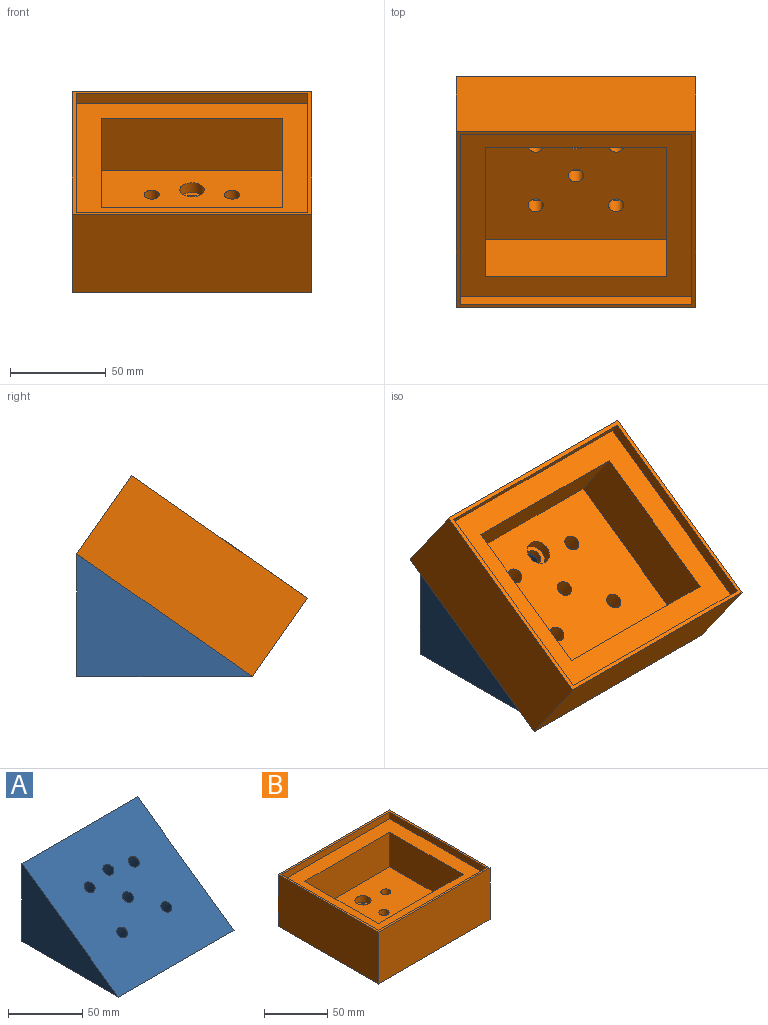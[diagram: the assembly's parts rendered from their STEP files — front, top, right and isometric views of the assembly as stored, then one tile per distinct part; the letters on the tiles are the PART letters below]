
ASSEMBLY  parts=2 mates=1
PART A: 34 faces, bbox 110x91.8x64.2 mm
  f0: plane 60x36mm, normal (0,0,-1), area 1964.4mm2, adj f5,f10,f11,f12,f21,f22,f23,f24
  f1: cylinder r=4mm len=21.79mm, axis (0,-0.57,0.82), area 481.3mm2, adj f7,f26,f30,f31
  f2: cylinder r=4mm len=21.79mm, axis (0,-0.57,0.82), area 481.3mm2, adj f7,f27,f28,f29
  f3: plane 110x64.24mm, normal (0,1,0), area 7040.8mm2, adj f6,f7,f8,f9,f17,f18,f19,f20
  f4: plane 13x6.5mm, normal (0,-1,0), area 58.5mm2, adj f13,f14,f15,f16,f17,f18,f19,f20
  f5: plane 60x18mm, normal (0,-1,0), area 995.5mm2, adj f0,f6,f11,f12,f13,f14,f15,f16
  f6: plane 110x91.75mm, normal (0,0,-1), area 7932.5mm2, adj f3,f5,f7,f8,f9,f10,f11,f12
  f7: plane 110x91.75mm, normal (0,-0.57,0.82), area 12017.4mm2, adj f1,f2,f3,f6,f8,f9,f21,f23
  f8: plane 91.75x64.24mm, normal (1,0,0), area 2947.2mm2, adj f3,f6,f7
  f9: plane 91.75x64.24mm, normal (-1,0,0), area 2947.2mm2, adj f3,f6,f7
  f10: plane 60x18mm, normal (0,1,0), area 979.5mm2, adj f0,f6,f11,f12,f29,f31
  f11: plane 36x18mm, normal (1,0,0), area 648mm2, adj f0,f5,f6,f10
  f12: plane 36x18mm, normal (-1,0,0), area 648mm2, adj f0,f5,f6,f10
  f13: plane 13x7mm, normal (0,0,-1), area 91mm2, adj f4,f5,f14,f16
  f14: plane 7x6.5mm, normal (1,0,0), area 45.5mm2, adj f4,f5,f13,f15
  f15: plane 13x7mm, normal (0,0,1), area 91mm2, adj f4,f5,f14,f16
  f16: plane 7x6.5mm, normal (-1,0,0), area 45.5mm2, adj f4,f5,f13,f15
  f17: plane 8x0.33mm, normal (0,0,-1), area 2.7mm2, adj f3,f4,f18,f20
  f18: plane 3.25x0.33mm, normal (-1,0,0), area 1.1mm2, adj f3,f4,f17,f19
  f19: plane 8x0.33mm, normal (0,0,1), area 2.7mm2, adj f3,f4,f18,f20
  f20: plane 3.25x0.33mm, normal (1,0,0), area 1.1mm2, adj f3,f4,f17,f19
  f21: cylinder r=4mm len=21.02mm, axis (0,-0.57,0.82), area 432.7mm2, adj f0,f7
  f22: cone r=0mm half-angle=59deg, axis (0,-0.57,0.82), area 13.1mm2, adj f0,f23
  f23: cylinder r=4mm len=29.98mm, axis (0,-0.57,0.82), area 749.4mm2, adj f0,f7,f22
  f24: cone r=0mm half-angle=59deg, axis (0,-0.57,0.82), area 13.1mm2, adj f0,f25
  f25: cylinder r=4mm len=29.98mm, axis (0,-0.57,0.82), area 749.4mm2, adj f0,f7,f24
  f26: cone r=0mm half-angle=59deg, axis (0,-0.57,0.82), area 58.6mm2, adj f1
  f27: cone r=0mm half-angle=59deg, axis (0,-0.57,0.82), area 58.6mm2, adj f2
  f28: cone r=0mm half-angle=59deg, axis (0,1,0), area 19.1mm2, adj f2,f29
  f29: cylinder r=4mm len=8mm, axis (0,1,0), area 180.4mm2, adj f2,f10,f28
  f30: cone r=0mm half-angle=59deg, axis (0,1,0), area 19mm2, adj f1,f31
  f31: cylinder r=4mm len=8mm, axis (0,1,0), area 180.4mm2, adj f1,f10,f30
  f32: plane 8x4.07mm, normal (0,0,1), area 24.4mm2, adj f5,f33
  f33: cylinder r=4.06mm len=34.17mm, axis (0,-0.57,0.82), area 846.9mm2, adj f0,f7,f32
PART B: 24 faces, bbox 125x112x50 mm
  f0: plane 125x112mm, normal (0,0,1), area 932mm2, adj f1,f2,f3,f4,f6,f7,f8,f9
  f1: plane 125x50mm, normal (0,-1,0), area 6250mm2, adj f0,f2,f4,f5
  f2: plane 112x50mm, normal (1,0,0), area 5600mm2, adj f0,f1,f3,f5
  f3: plane 125x50mm, normal (0,1,0), area 6250mm2, adj f0,f2,f4,f5
  f4: plane 112x50mm, normal (-1,0,0), area 5600mm2, adj f0,f1,f3,f5
  f5: plane 125x112mm, normal (0,0,-1), area 13696.8mm2, adj f1,f2,f3,f4,f16,f17,f18,f19
  f6: plane 108x6.5mm, normal (1,0,0), area 702mm2, adj f0,f7,f9,f10
  f7: plane 121x6.5mm, normal (0,1,0), area 786.5mm2, adj f0,f6,f8,f10
  f8: plane 108x6.5mm, normal (-1,0,0), area 702mm2, adj f0,f7,f9,f10
  f9: plane 121x6.5mm, normal (0,-1,0), area 786.5mm2, adj f0,f6,f8,f10
  f10: plane 121x108mm, normal (0,0,1), area 5278mm2, adj f6,f7,f8,f9,f11,f12,f13,f14
  f11: plane 82x33.5mm, normal (1,0,0), area 2747mm2, adj f10,f12,f14,f15
  f12: plane 95x33.5mm, normal (0,1,0), area 3182.5mm2, adj f10,f11,f13,f15
  f13: plane 82x33.5mm, normal (-1,0,0), area 2747mm2, adj f10,f12,f14,f15
  f14: plane 95x33.5mm, normal (0,-1,0), area 3182.5mm2, adj f10,f11,f13,f15
  f15: plane 95x82mm, normal (0,0,1), area 7411mm2, adj f11,f12,f13,f14,f16,f17,f18,f19
  f16: cylinder r=4mm len=10mm, axis (0,0,1), area 251.3mm2, adj f5,f15
  f17: cylinder r=4mm len=10mm, axis (0,0,1), area 251.3mm2, adj f5,f15
  f18: cylinder r=4mm len=10mm, axis (0,0,1), area 251.3mm2, adj f5,f15
  f19: cylinder r=4mm len=10mm, axis (0,0,1), area 251.3mm2, adj f5,f15
  f20: cylinder r=4mm len=10mm, axis (0,0,1), area 251.3mm2, adj f5,f15
  f21: cylinder r=6.38mm len=12.75mm, axis (0,0,1), area 250.3mm2, adj f15,f22
  f22: plane 12.75x12.75mm, normal (0,0,1), area 75.8mm2, adj f21,f23
  f23: cylinder r=4.06mm len=8.13mm, axis (0,0,1), area 95.8mm2, adj f5,f22
PLACE A at identity fixed
PLACE B rot(axis=(1,0,0),35deg) t=(0,-15.23,32.12)mm
MATE fastened A.f7 <-> B.f5  axis (0,-0.57,0.82) through (0,30.64,64.24)mm
